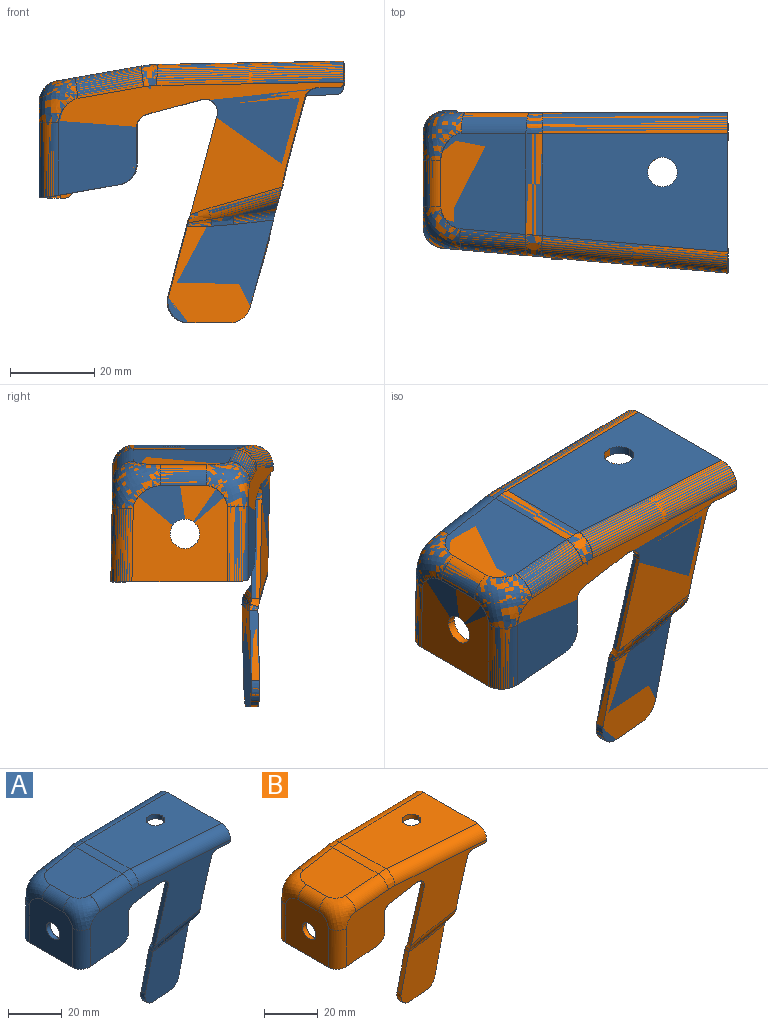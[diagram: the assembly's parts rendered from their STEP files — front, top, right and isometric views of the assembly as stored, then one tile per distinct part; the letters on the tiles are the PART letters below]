
ASSEMBLY  parts=2 mates=1
PART A: 90 faces, bbox 75.4x41.3x64.8 mm
  f0: bspline ~3.56x2.8mm, area 6.4mm2, adj f1,f6,f8,f9
  f1: bspline ~20.65x5.71mm, area 43.2mm2, adj f0,f2,f7,f10
  f2: extruded ~5x3.71mm, area 13.1mm2, adj f1,f3,f7,f10
  f3: plane 9.84x2.84mm, normal (0,0,-1), area 19.4mm2, adj f2,f4,f7,f10
  f4: extruded ~6.29x5.17mm, area 18.4mm2, adj f3,f5,f7,f10
  f5: plane 16.55x4.61mm, normal (-0.96,-0.08,0.26), area 34.3mm2, adj f4,f7,f10,f11
  f6: cylinder r=3mm len=10.3mm, axis (0.99,0.09,0.11), area 23mm2, adj f0,f7,f12,f13
  f7: plane 25.33x24.65mm, normal (0.09,-1,0), area 456.8mm2, adj f1,f2,f3,f4,f5,f6,f13,f14
  f8: cylinder r=5mm len=10.41mm, axis (0.99,0.09,0.11), area 38.3mm2, adj f0,f10,f15,f16
  f9: bspline ~3.35x3.24mm, area 5.4mm2, adj f0,f12,f15,f17
  f10: plane 26.1x25.42mm, normal (-0.09,1,0), area 466.1mm2, adj f1,f2,f3,f4,f5,f8,f16,f18
  f11: bspline ~2.11x1.5mm, area 2.5mm2, adj f5,f14,f18,f19
  f12: plane 10.67x3.07mm, normal (0.14,-0.7,-0.7), area 13.6mm2, adj f6,f9,f20
  f13: bspline ~5.42x2.51mm, area 10.9mm2, adj f6,f7,f14,f20
  f14: bspline ~5.72x1.76mm, area 7.7mm2, adj f7,f11,f13,f21
  f15: plane 10.99x3.4mm, normal (-0.14,0.7,0.7), area 13.5mm2, adj f8,f9,f22
  f16: bspline ~5.32x3.88mm, area 17.9mm2, adj f8,f10,f18,f22
  f17: bspline ~3.68x2.89mm, area 7mm2, adj f9,f20,f22,f23
  f18: bspline ~5.72x2.93mm, area 12.8mm2, adj f10,f11,f16,f34
  f19: bspline ~2.24x1.95mm, area 3.6mm2, adj f11,f21,f33,f34
  f20: cylinder r=4.5mm len=18.52mm, axis (0.96,-0.08,0.28), area 60.8mm2, adj f12,f13,f17,f21,f36
  f21: bspline ~6.18x3.37mm, area 11.3mm2, adj f14,f19,f20,f36
  f22: cylinder r=2.5mm len=18.07mm, axis (0.96,-0.08,0.28), area 33.8mm2, adj f15,f16,f17,f34,f38
  f23: plane 4.7x2.08mm, normal (0.97,-0.09,-0.21), area 9.6mm2, adj f17,f24,f36,f38
  f24: plane 16.62x4.63mm, normal (0.96,-0.08,-0.26), area 34.4mm2, adj f23,f25,f36,f38
  f25: extruded ~3.02x2.24mm, area 7.8mm2, adj f24,f26,f36,f38
  f26: plane 5.6x2.47mm, normal (0.02,0,-1), area 10.9mm2, adj f25,f35,f36,f38
  f27: plane 14.51x3.25mm, normal (0.17,-0.02,-0.98), area 29.2mm2, adj f28,f36,f37,f38
  f28: extruded ~4.92x4.31mm, area 14mm2, adj f27,f29,f36,f38
  f29: plane 8.78x1.99mm, normal (1,-0.09,0), area 17.6mm2, adj f28,f30,f36,f38
  f30: extruded ~2.9x2.4mm, area 7.9mm2, adj f29,f31,f36,f38
  f31: plane 13.35x3.53mm, normal (0.26,-0.02,-0.97), area 27.4mm2, adj f30,f32,f36,f38
  f32: extruded ~3.95x3.78mm, area 12.6mm2, adj f31,f33,f36,f38
  f33: plane 23.53x6.48mm, normal (-0.96,0.08,0.26), area 48.7mm2, adj f19,f32,f36,f38
  f34: bspline ~5.94x2.8mm, area 6.4mm2, adj f18,f19,f22,f38
  f35: cylinder r=1mm len=2.08mm, axis (-0.09,-1,0), area 3.1mm2, adj f26,f36,f38,f39
  f36: plane 70.14x33.88mm, normal (-0.09,-1,0), area 1067.6mm2, adj f20,f21,f23,f24,f25,f26,f27,f28
  f37: bspline ~4.98x4.74mm, area 12mm2, adj f27,f40,f45,f46
  f38: plane 69.76x33.5mm, normal (0.09,1,0), area 1068.3mm2, adj f22,f23,f24,f25,f26,f27,f28,f29
  f39: plane 1.99x0.22mm, normal (1,-0.09,0), area 0.4mm2, adj f35,f36,f38,f55
  f40: cylinder r=5mm len=17.85mm, axis (0,0,-1), area 130.1mm2, adj f36,f37,f42,f57
  f41: cylinder r=5mm len=16.1mm, axis (0.98,-0.09,0.17), area 121.4mm2, adj f36,f42,f43,f58
  f42: bspline ~15.47x13.56mm, area 155.1mm2, adj f36,f40,f41,f56,f57,f58
  f43: bspline ~5.3x5.25mm, area 28.5mm2, adj f36,f41,f44,f59
  f44: cylinder r=5mm len=44.65mm, axis (1,-0.09,0.02), area 347.5mm2, adj f36,f43,f55,f60
  f45: plane 22.58x2mm, normal (0,0,-1), area 45.1mm2, adj f37,f57,f61,f63
  f46: cylinder r=3mm len=17.85mm, axis (0,0,-1), area 77.3mm2, adj f37,f38,f50,f63
  f47: cylinder r=3.5mm len=7mm, axis (-1,0,0), area 22mm2, adj f48,f57,f63
  f48: cylinder r=3.5mm len=7mm, axis (-1,0,0), area 22mm2, adj f47,f57,f63
  f49: cylinder r=3mm len=15.88mm, axis (0.98,-0.09,0.17), area 72.8mm2, adj f38,f50,f51,f64
  f50: bspline ~13.21x11.26mm, area 95.3mm2, adj f38,f46,f49,f62,f63,f64
  f51: bspline ~3.65x3.3mm, area 16.2mm2, adj f38,f49,f52,f65
  f52: cylinder r=3mm len=44.51mm, axis (1,-0.09,0.02), area 208.5mm2, adj f38,f51,f55,f66
  f53: cylinder r=3.5mm len=7.04mm, axis (0.02,0,-1), area 22mm2, adj f54,f60,f66
  f54: cylinder r=3.5mm len=7.04mm, axis (0.02,0,-1), area 22mm2, adj f53,f60,f66
  f55: bspline ~5.03x5.01mm, area 12.6mm2, adj f39,f44,f52,f67
  f56: cylinder r=5mm len=10.93mm, axis (0,1,0), area 76.3mm2, adj f42,f57,f58,f69
  f57: plane 25.44x25.22mm, normal (-1,0,0), area 456.9mm2, adj f40,f42,f45,f47,f48,f56,f68,f69
  f58: plane 26.49x22.75mm, normal (-0.17,0,0.98), area 459mm2, adj f41,f42,f56,f59,f69,f70
  f59: cylinder r=25.02mm len=24.16mm, axis (0,1,0), area 94.3mm2, adj f43,f58,f60,f71
  f60: plane 43.94x28mm, normal (-0.02,0,1), area 1107.7mm2, adj f44,f53,f54,f59,f67,f72
  f61: bspline ~5.08x5.08mm, area 12.6mm2, adj f45,f68,f78,f79
  f62: cylinder r=3mm len=10.93mm, axis (0,1,0), area 45.8mm2, adj f50,f63,f64,f80
  f63: plane 25.59x25.37mm, normal (1,0,0), area 453mm2, adj f45,f46,f47,f48,f50,f62,f79,f80
  f64: plane 26.64x22.9mm, normal (0.17,0,-0.98), area 453.2mm2, adj f49,f50,f62,f65,f80,f81
  f65: cylinder r=23.01mm len=24.16mm, axis (0,1,0), area 86.8mm2, adj f51,f64,f66,f82
  f66: plane 45.5x29.56mm, normal (0.02,0,-1), area 1104.1mm2, adj f52,f53,f54,f65,f67,f83
  f67: bspline ~28x2.02mm, area 56.2mm2, adj f55,f60,f66,f84
  f68: cylinder r=5mm len=17.48mm, axis (0,-0.02,1), area 136.2mm2, adj f57,f61,f69,f85
  f69: bspline ~15.87x15mm, area 168.1mm2, adj f56,f57,f58,f68,f70,f85
  f70: cylinder r=5mm len=16.18mm, axis (-0.98,0,-0.17), area 120.8mm2, adj f58,f69,f71,f85
  f71: bspline ~5.21x5mm, area 28.3mm2, adj f59,f70,f72,f85
  f72: cylinder r=5mm len=44.03mm, axis (-1,0,-0.02), area 341mm2, adj f60,f71,f84,f85
  f73: extruded ~2.66x2mm, area 5.3mm2, adj f74,f85,f86,f87
  f74: plane 15.31x2.74mm, normal (0.17,0.02,-0.98), area 31.1mm2, adj f73,f75,f85,f87
  f75: extruded ~3.43x2.39mm, area 8.8mm2, adj f74,f76,f85,f87
  f76: plane 15.42x2.27mm, normal (1,0,0), area 30.8mm2, adj f75,f77,f85,f87
  f77: cylinder r=2mm len=2.03mm, axis (0,1,0.02), area 6.3mm2, adj f76,f78,f85,f87
  f78: plane 2x1mm, normal (0,0.02,-1), area 2mm2, adj f61,f77,f85,f87
  f79: cylinder r=3mm len=17.44mm, axis (0,-0.02,1), area 81.7mm2, adj f61,f63,f80,f87
  f80: bspline ~13.59x12.59mm, area 117.8mm2, adj f62,f63,f64,f79,f81,f87
  f81: cylinder r=3mm len=15.83mm, axis (-0.98,0,-0.17), area 72.5mm2, adj f64,f80,f82,f87
  f82: bspline ~3.64x3.25mm, area 16mm2, adj f65,f81,f83,f87
  f83: cylinder r=3mm len=44mm, axis (-1,0,-0.02), area 204.6mm2, adj f66,f82,f84,f87
  f84: bspline ~5x4.95mm, area 12.4mm2, adj f67,f72,f83,f88
  f85: plane 69.92x30.26mm, normal (0,1,0.02), area 258.3mm2, adj f68,f69,f70,f71,f72,f73,f74,f75
  f86: plane 41.84x2mm, normal (0.02,0.02,-1), area 83.7mm2, adj f73,f85,f87,f89
  f87: plane 69.53x29.87mm, normal (0,-1,-0.02), area 257.8mm2, adj f73,f74,f75,f76,f77,f78,f79,f80
  f88: bspline ~2.04x1.07mm, area 2.1mm2, adj f84,f85,f87,f89
  f89: cylinder r=2mm len=2.03mm, axis (0,1,0.02), area 6.2mm2, adj f85,f86,f87,f88
PART B: 90 faces, bbox 75.8x41.7x65.2 mm
  f0: cylinder r=2mm len=2.03mm, axis (0,1,0.02), area 6.2mm2, adj f1,f2,f18,f19
  f1: bspline ~2.02x1.07mm, area 2.1mm2, adj f0,f2,f15,f18
  f2: plane 69.53x29.87mm, normal (0,-1,-0.02), area 257mm2, adj f0,f1,f3,f4,f5,f6,f7,f8
  f3: extruded ~2.66x2mm, area 5.3mm2, adj f2,f4,f18,f19
  f4: plane 15.31x2.74mm, normal (0.17,0.02,-0.98), area 31.1mm2, adj f2,f3,f5,f18
  f5: extruded ~3.43x2.39mm, area 8.8mm2, adj f2,f4,f6,f18
  f6: plane 15.42x2.27mm, normal (1,0,0), area 30.8mm2, adj f2,f5,f7,f18
  f7: cylinder r=2mm len=2.03mm, axis (0,1,0.02), area 6.3mm2, adj f2,f6,f8,f18
  f8: plane 2x1mm, normal (0,0.02,-1), area 2mm2, adj f2,f7,f9,f18
  f9: bspline ~5.08x5.08mm, area 12.6mm2, adj f8,f10,f30,f31
  f10: cylinder r=3mm len=17.44mm, axis (0,-0.02,1), area 81.7mm2, adj f2,f9,f11,f41
  f11: bspline ~13.59x12.59mm, area 117.8mm2, adj f2,f10,f12,f40,f41,f44
  f12: cylinder r=3mm len=15.83mm, axis (-0.98,0,-0.17), area 72.5mm2, adj f2,f11,f13,f44
  f13: bspline ~3.64x3.25mm, area 16mm2, adj f2,f12,f14,f42
  f14: cylinder r=3mm len=44mm, axis (-1,0,-0.02), area 204.6mm2, adj f2,f13,f15,f43
  f15: bspline ~5x4.95mm, area 12.4mm2, adj f1,f14,f16,f36
  f16: cylinder r=5mm len=44.03mm, axis (-1,0,-0.02), area 341mm2, adj f15,f17,f18,f56
  f17: bspline ~5.21x5mm, area 28.3mm2, adj f16,f18,f37,f55
  f18: plane 69.92x30.26mm, normal (0,1,0.02), area 256.9mm2, adj f0,f1,f3,f4,f5,f6,f7,f8
  f19: plane 41.84x2mm, normal (0.02,0.02,-1), area 83.7mm2, adj f0,f2,f3,f18
  f20: extruded ~6.29x5.17mm, area 18.4mm2, adj f21,f22,f26,f35
  f21: plane 9.84x2.84mm, normal (0,0,-1), area 19.4mm2, adj f20,f22,f26,f32
  f22: plane 25.42x24.74mm, normal (-0.09,1,0), area 459.9mm2, adj f20,f21,f23,f24,f32,f35,f39,f45
  f23: cylinder r=5mm len=10.41mm, axis (0.99,0.09,0.11), area 38.3mm2, adj f22,f45,f46,f47
  f24: bspline ~20.65x5.71mm, area 43.2mm2, adj f22,f26,f32,f47
  f25: cylinder r=3mm len=10.3mm, axis (0.99,0.09,0.11), area 23mm2, adj f26,f47,f48,f49
  f26: plane 25.04x24.36mm, normal (0.09,-1,0), area 456.8mm2, adj f20,f21,f24,f25,f32,f35,f48,f50
  f27: bspline ~2.11x1.5mm, area 2.5mm2, adj f35,f39,f50,f51
  f28: cylinder r=3.5mm len=7mm, axis (-1,0,0), area 22mm2, adj f29,f41,f54
  f29: cylinder r=3.5mm len=7mm, axis (-1,0,0), area 22mm2, adj f28,f41,f54
  f30: cylinder r=5mm len=17.48mm, axis (0,-0.02,1), area 136.2mm2, adj f9,f18,f38,f54
  f31: plane 22.58x2mm, normal (0,0,-1), area 45.2mm2, adj f9,f41,f52,f54
  f32: extruded ~5x3.71mm, area 13.1mm2, adj f21,f22,f24,f26
  f33: cylinder r=3.5mm len=7.04mm, axis (0.02,0,-1), area 22mm2, adj f34,f43,f56
  f34: cylinder r=3.5mm len=7.04mm, axis (0.02,0,-1), area 22mm2, adj f33,f43,f56
  f35: plane 16.55x4.61mm, normal (-0.96,-0.08,0.26), area 34.3mm2, adj f20,f22,f26,f27
  f36: bspline ~28x2mm, area 56.2mm2, adj f15,f43,f56,f57
  f37: cylinder r=5mm len=16.18mm, axis (-0.98,0,-0.17), area 120.8mm2, adj f17,f18,f38,f58
  f38: bspline ~15.87x15mm, area 186.2mm2, adj f18,f30,f37,f53,f54,f58
  f39: bspline ~5.72x2.88mm, area 12.8mm2, adj f22,f27,f45,f59
  f40: cylinder r=3mm len=10.93mm, axis (0,1,0), area 45.8mm2, adj f11,f41,f44,f61
  f41: plane 25.59x25.37mm, normal (1,0,0), area 456.9mm2, adj f10,f11,f28,f29,f31,f40,f60,f61
  f42: cylinder r=23mm len=24.16mm, axis (0,1,0), area 86.8mm2, adj f13,f43,f44,f62
  f43: plane 44.3x28.36mm, normal (0.02,0,-1), area 1104mm2, adj f14,f33,f34,f36,f42,f63
  f44: plane 26.64x22.9mm, normal (0.17,0,-0.98), area 458.9mm2, adj f11,f12,f40,f42,f61,f64
  f45: bspline ~5.33x3.91mm, area 17.9mm2, adj f22,f23,f39,f65
  f46: plane 10.72x3.12mm, normal (-0.14,0.7,0.7), area 13.6mm2, adj f23,f65,f66
  f47: bspline ~3.56x2.8mm, area 6.4mm2, adj f23,f24,f25,f66
  f48: bspline ~5.31x2.49mm, area 10.9mm2, adj f25,f26,f50,f67
  f49: plane 10.67x3.07mm, normal (0.14,-0.7,-0.7), area 13.6mm2, adj f25,f66,f67
  f50: bspline ~5.72x1.76mm, area 7.7mm2, adj f26,f27,f48,f68
  f51: bspline ~2.22x1.95mm, area 3.6mm2, adj f27,f59,f68,f69
  f52: bspline ~4.98x4.74mm, area 12mm2, adj f31,f60,f75,f76
  f53: cylinder r=5mm len=10.93mm, axis (0,1,0), area 76.3mm2, adj f38,f54,f58,f77
  f54: plane 26.02x25.81mm, normal (-1,0,0), area 456.9mm2, adj f28,f29,f30,f31,f38,f53,f76,f77
  f55: cylinder r=25mm len=24.16mm, axis (0,1,0), area 94.3mm2, adj f17,f56,f58,f78
  f56: plane 43.94x28mm, normal (-0.02,0,1), area 1107.7mm2, adj f16,f33,f34,f36,f55,f79
  f57: bspline ~5.01x4.99mm, area 12.6mm2, adj f36,f63,f79,f80
  f58: plane 27x23.25mm, normal (-0.17,0,0.98), area 458.9mm2, adj f37,f38,f53,f55,f77,f83
  f59: bspline ~5.83x2.78mm, area 6.4mm2, adj f39,f51,f65,f85
  f60: cylinder r=3mm len=17.85mm, axis (0,0,-1), area 78mm2, adj f41,f52,f61,f85
  f61: bspline ~13.19x11.25mm, area 95.3mm2, adj f40,f41,f44,f60,f64,f85
  f62: bspline ~3.65x3.35mm, area 16.2mm2, adj f42,f63,f64,f85
  f63: cylinder r=3mm len=44.51mm, axis (1,-0.09,0.02), area 208.5mm2, adj f43,f57,f62,f85
  f64: cylinder r=3mm len=15.88mm, axis (0.98,-0.09,0.17), area 74mm2, adj f44,f61,f62,f85
  f65: cylinder r=2.5mm len=18.07mm, axis (0.96,-0.08,0.28), area 33.8mm2, adj f45,f46,f59,f85,f86
  f66: bspline ~3.36x3.25mm, area 5.4mm2, adj f46,f47,f49,f86
  f67: cylinder r=4.5mm len=18.52mm, axis (0.96,-0.08,0.28), area 60.8mm2, adj f48,f49,f68,f86,f87
  f68: bspline ~6.18x3.37mm, area 11.3mm2, adj f50,f51,f67,f87
  f69: plane 23.53x6.48mm, normal (-0.96,0.08,0.26), area 48.7mm2, adj f51,f70,f85,f87
  f70: extruded ~3.95x3.78mm, area 12.6mm2, adj f69,f71,f85,f87
  f71: plane 13.35x3.53mm, normal (0.26,-0.02,-0.97), area 27.4mm2, adj f70,f72,f85,f87
  f72: extruded ~2.9x2.4mm, area 7.9mm2, adj f71,f73,f85,f87
  f73: plane 8.78x1.99mm, normal (1,-0.09,0), area 17.6mm2, adj f72,f74,f85,f87
  f74: extruded ~4.92x4.31mm, area 14mm2, adj f73,f75,f85,f87
  f75: plane 14.51x3.25mm, normal (0.17,-0.02,-0.98), area 29.2mm2, adj f52,f74,f85,f87
  f76: cylinder r=5mm len=17.85mm, axis (0,0,-1), area 130.1mm2, adj f52,f54,f77,f87
  f77: bspline ~15.47x13.56mm, area 155.1mm2, adj f53,f54,f58,f76,f83,f87
  f78: bspline ~5.3x5.25mm, area 28.5mm2, adj f55,f79,f83,f87
  f79: cylinder r=5mm len=44.65mm, axis (1,-0.09,0.02), area 347.5mm2, adj f56,f57,f78,f87
  f80: plane 1.99x0.22mm, normal (1,-0.09,0), area 0.4mm2, adj f57,f81,f85,f87
  f81: cylinder r=1mm len=2.08mm, axis (-0.09,-1,0), area 3.1mm2, adj f80,f82,f85,f87
  f82: plane 5.6x2.47mm, normal (0.02,0,-1), area 10.9mm2, adj f81,f84,f85,f87
  f83: cylinder r=5mm len=16.1mm, axis (0.98,-0.09,0.17), area 123.4mm2, adj f58,f77,f78,f87
  f84: extruded ~3.02x2.24mm, area 7.8mm2, adj f82,f85,f87,f88
  f85: plane 69.76x33.5mm, normal (0.09,1,0), area 1067.4mm2, adj f59,f60,f61,f62,f63,f64,f65,f69
  f86: bspline ~3.68x2.89mm, area 7mm2, adj f65,f66,f67,f89
  f87: plane 70.14x33.88mm, normal (-0.09,-1,0), area 1067.3mm2, adj f67,f68,f69,f70,f71,f72,f73,f74
  f88: plane 16.62x4.63mm, normal (0.96,-0.08,-0.26), area 34.4mm2, adj f84,f85,f87,f89
  f89: plane 4.7x2.08mm, normal (0.97,-0.09,-0.21), area 9.6mm2, adj f85,f86,f87,f88
PLACE A t=(154.2,-508.48,-110.08)mm
PLACE B t=(154.2,-508.48,-110.08)mm
MATE fastened B.f56 <-> A.f60  axis (-0.02,0,1) through (-452.48,-44.6,367.56)mm
